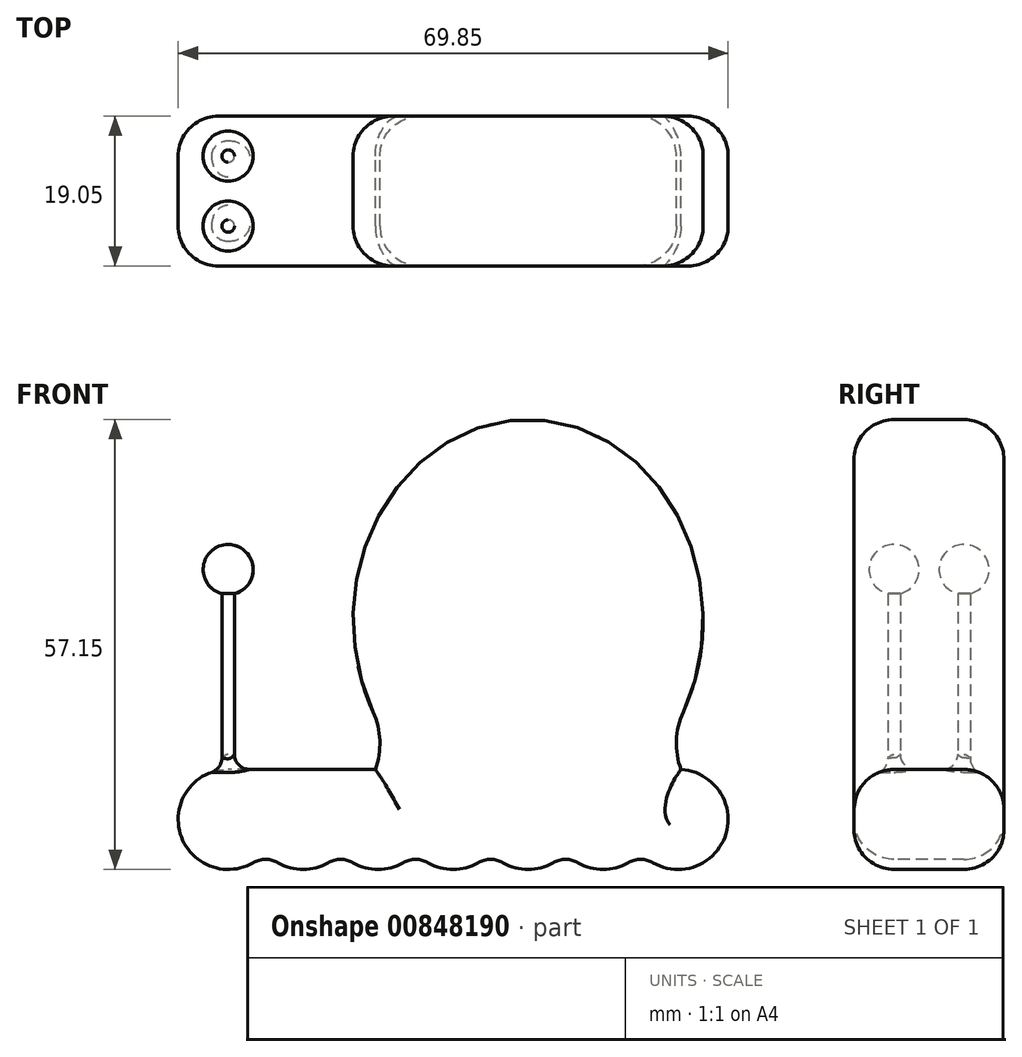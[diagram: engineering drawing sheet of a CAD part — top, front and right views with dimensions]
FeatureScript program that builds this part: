
annotation { "Feature Type Name" : "Feature", "Feature Type Description" : "" }
export const myFeature = defineFeature(function(context is Context, id is Id, definition is map)
    precondition{}
    {
        {
            var Q0;
            Q0=qCreatedBy(makeId("Front.planeOp"),FACE);
            var sketch = newSketch(context, id + "F0", { "sketchPlane" : qUnion([Q0])});
            skEllipticalArc(sketch, "E0", {});
            skLineSegment(sketch, "E1", {"start": v(0, 0) * mm, "end": v(-18.88, 0) * mm});
            skLineSegment(sketch, "E2", {"start": v(0, 0) * mm, "end": v(18.88, 0) * mm});
            skArc(sketch, "E3", {"start": v(19.7, 13.64) * mm, "mid": v(18.89, 8.58) * mm, "end": v(20.78, 3.82) * mm});
            skArc(sketch, "E4", {"start": v(-20.78, 3.82) * mm, "mid": v(-18.89, 8.58) * mm, "end": v(-19.7, 13.64) * mm});
            skPoint(sketch, "E5.end.orphan", {"position": v(-22.23, 25.4) * mm});
            skPoint(sketch, "E6.orphan", {"position": v(0, 50.8) * mm});
            skPoint(sketch, "E7.visualSharp", {"position": v(-28.46, 0) * mm});
            skArc(sketch, "E7.filletArc", {"start": v(-20.78, 3.82) * mm, "mid": v(-21.02, 1.32) * mm, "end": v(-18.88, 0) * mm});
            skPoint(sketch, "E8.visualSharp", {"position": v(28.46, 0) * mm});
            skArc(sketch, "E8.filletArc", {"start": v(18.88, 0) * mm, "mid": v(21.02, 1.32) * mm, "end": v(20.78, 3.82) * mm});
            skArc(sketch, "E9", {"start": v(-6.35, 0) * mm, "mid": v(0, -6.35) * mm, "end": v(6.35, 0) * mm});
            skArc(sketch, "E10.1.0.0", {"start": v(3.17, 0) * mm, "mid": v(9.52, -6.35) * mm, "end": v(15.88, 0) * mm});
            skArc(sketch, "E10.2.0.0", {"start": v(12.7, 0) * mm, "mid": v(23.41, -4.62) * mm, "end": v(19.4, 6.34) * mm});
            skLineSegment(sketch, "E10.direction1", {"start": v(0, 0) * mm, "end": v(9.53, 0) * mm, "construction": true});
            skArc(sketch, "E11.1.0.0", {"start": v(-15.88, 0) * mm, "mid": v(-9.53, -6.35) * mm, "end": v(-3.17, 0) * mm});
            skArc(sketch, "E11.2.0.0", {"start": v(-19.4, 6.34) * mm, "mid": v(-23.41, -4.62) * mm, "end": v(-12.7, 0) * mm});
            skCircle(sketch, "E11.3.0.0", {"center": v(-28.58, 0) * mm, "radius": 6.35 * mm});
            skCircle(sketch, "E11.4.0.0", {"center": v(-38.1, 0) * mm, "radius": 6.35 * mm});
            skLineSegment(sketch, "E11.direction1", {"start": v(0, 0) * mm, "end": v(-9.53, 0) * mm, "construction": true});
            skLineSegment(sketch, "E12", {"start": v(-38.1, 6.35) * mm, "end": v(-19.4, 6.35) * mm});
            const initialGuessF0  = {"E0": [0, 0.0254, 0, 1, 0.0254, 0.022225, 4.23107215542133, 2.0521131517582556]};
            skSetInitialGuess(sketch, initialGuessF0);
            skSolve(sketch);
        }
        {
            var Q0;
            {var subQ15=sQuery(id+"F0.wireOp",EDGE,"E0");Q0=makeQuery(id+"F0.imprint","IMPRINT",FACE,{"disambiguationData":[TD([[makeQuery(id+"F0.imprint","IMPRINT",EDGE,{"derivedFrom":subQ15}),1.0]])]});}
            var Q1;
            {var subQ5=sQuery(id+"F0.wireOp",EDGE,"E8.filletArc");Q1=makeQuery(id+"F0.imprint","IMPRINT",FACE,{"disambiguationData":[TD([[makeQuery(id+"F0.imprint","IMPRINT",EDGE,{"derivedFrom":subQ5}),-1.0]])]});}
            var Q2;
            {var subQ0=sQuery(id+"F0.wireOp",EDGE,"E10.1.0.0");var subQ1=sQuery(id+"F0.wireOp",EDGE,"E2");var subQ2=makeQuery(id+"F0.imprint","INTERSECT",VERTEX,{"disambiguationData":[OD(1.0)],"derivedFrom":[subQ1,subQ0]});Q2=makeQuery(id+"F0.imprint","IMPRINT",FACE,{"disambiguationData":[TD([[makeQuery(id+"F0.imprint","IMPRINT",EDGE,{"disambiguationData":[TD([[subQ2,1.0]])],"derivedFrom":subQ1}),-1.0]])]});}
            var Q3;
            {var subQ0=sQuery(id+"F0.wireOp",EDGE,"E9");var subQ1=sQuery(id+"F0.wireOp",EDGE,"E2");var subQ2=makeQuery(id+"F0.imprint","INTERSECT",VERTEX,{"derivedFrom":[subQ1,subQ0]});Q3=makeQuery(id+"F0.imprint","IMPRINT",FACE,{"disambiguationData":[TD([[makeQuery(id+"F0.imprint","IMPRINT",EDGE,{"disambiguationData":[TD([[subQ2,-1.0]])],"derivedFrom":subQ1}),-1.0]])]});}
            var Q4;
            {var subQ0=sQuery(id+"F0.wireOp",EDGE,"E9");var subQ1=sQuery(id+"F0.wireOp",EDGE,"E2");var subQ2=makeQuery(id+"F0.imprint","INTERSECT",VERTEX,{"derivedFrom":[subQ1,subQ0]});Q4=makeQuery(id+"F0.imprint","IMPRINT",FACE,{"disambiguationData":[TD([[makeQuery(id+"F0.imprint","IMPRINT",EDGE,{"disambiguationData":[TD([[subQ2,1.0]])],"derivedFrom":subQ1}),-1.0]])]});}
            var Q5;
            {var subQ5=sQuery(id+"F0.wireOp",EDGE,"E2");var subQ7=sQuery(id+"F0.wireOp",EDGE,"E1");var subQ8=makeQuery(id+"F0.imprint","INTERSECT",VERTEX,{"derivedFrom":[subQ7,subQ5]});Q5=makeQuery(id+"F0.imprint","IMPRINT",FACE,{"disambiguationData":[TD([[makeQuery(id+"F0.imprint","IMPRINT",EDGE,{"disambiguationData":[TD([[subQ8,-1.0]])],"derivedFrom":subQ7}),1.0]])]});}
            var Q6;
            {var subQ0=sQuery(id+"F0.wireOp",EDGE,"E9");var subQ1=sQuery(id+"F0.wireOp",EDGE,"E1");var subQ2=makeQuery(id+"F0.imprint","INTERSECT",VERTEX,{"derivedFrom":[subQ1,subQ0]});Q6=makeQuery(id+"F0.imprint","IMPRINT",FACE,{"disambiguationData":[TD([[makeQuery(id+"F0.imprint","IMPRINT",EDGE,{"disambiguationData":[TD([[subQ2,1.0]])],"derivedFrom":subQ1}),1.0]])]});}
            var Q7;
            {var subQ0=sQuery(id+"F0.wireOp",EDGE,"E9");var subQ1=sQuery(id+"F0.wireOp",EDGE,"E1");var subQ2=makeQuery(id+"F0.imprint","INTERSECT",VERTEX,{"derivedFrom":[subQ1,subQ0]});Q7=makeQuery(id+"F0.imprint","IMPRINT",FACE,{"disambiguationData":[TD([[makeQuery(id+"F0.imprint","IMPRINT",EDGE,{"disambiguationData":[TD([[subQ2,-1.0]])],"derivedFrom":subQ1}),1.0]])]});}
            var Q8;
            {var subQ0=sQuery(id+"F0.wireOp",EDGE,"E11.1.0.0");var subQ1=sQuery(id+"F0.wireOp",EDGE,"E1");var subQ2=makeQuery(id+"F0.imprint","INTERSECT",VERTEX,{"disambiguationData":[OD(0.0)],"derivedFrom":[subQ1,subQ0]});Q8=makeQuery(id+"F0.imprint","IMPRINT",FACE,{"disambiguationData":[TD([[makeQuery(id+"F0.imprint","IMPRINT",EDGE,{"disambiguationData":[TD([[subQ2,1.0]])],"derivedFrom":subQ1}),1.0]])]});}
            var Q9;
            {var subQ8=sQuery(id+"F0.wireOp",EDGE,"E7.filletArc");Q9=makeQuery(id+"F0.imprint","IMPRINT",FACE,{"disambiguationData":[TD([[makeQuery(id+"F0.imprint","IMPRINT",EDGE,{"derivedFrom":subQ8}),-1.0]])]});}
            var Q10;
            {var subQ0=sQuery(id+"F0.wireOp",EDGE,"E11.3.0.0");var subQ1=sQuery(id+"F0.wireOp",EDGE,"E11.2.0.0");var subQ2=makeQuery(id+"F0.imprint","INTERSECT",VERTEX,{"disambiguationData":[OD(0.0)],"derivedFrom":[subQ1,subQ0]});Q10=makeQuery(id+"F0.imprint","IMPRINT",FACE,{"disambiguationData":[TD([[makeQuery(id+"F0.imprint","IMPRINT",EDGE,{"disambiguationData":[TD([[subQ2,1.0]])],"derivedFrom":subQ1}),1.0]])]});}
            var Q11;
            {var subQ0=sQuery(id+"F0.wireOp",EDGE,"E11.3.0.0");var subQ1=sQuery(id+"F0.wireOp",EDGE,"E11.2.0.0");var subQ2=makeQuery(id+"F0.imprint","INTERSECT",VERTEX,{"disambiguationData":[OD(0.0)],"derivedFrom":[subQ1,subQ0]});Q11=makeQuery(id+"F0.imprint","IMPRINT",FACE,{"disambiguationData":[TD([[makeQuery(id+"F0.imprint","IMPRINT",EDGE,{"disambiguationData":[TD([[subQ2,1.0]])],"derivedFrom":subQ1}),-1.0]])]});}
            var Q12;
            {var subQ0=sQuery(id+"F0.wireOp",EDGE,"E11.4.0.0");var subQ1=sQuery(id+"F0.wireOp",EDGE,"E11.3.0.0");var subQ2=makeQuery(id+"F0.imprint","INTERSECT",VERTEX,{"disambiguationData":[OD(0.0)],"derivedFrom":[subQ1,subQ0]});Q12=makeQuery(id+"F0.imprint","IMPRINT",FACE,{"disambiguationData":[TD([[makeQuery(id+"F0.imprint","IMPRINT",EDGE,{"disambiguationData":[TD([[subQ2,1.0]])],"derivedFrom":subQ1}),1.0]])]});}
            var Q13;
            {var subQ0=sQuery(id+"F0.wireOp",EDGE,"E11.4.0.0");var subQ1=sQuery(id+"F0.wireOp",EDGE,"E11.3.0.0");var subQ2=makeQuery(id+"F0.imprint","INTERSECT",VERTEX,{"disambiguationData":[OD(0.0)],"derivedFrom":[subQ1,subQ0]});Q13=makeQuery(id+"F0.imprint","IMPRINT",FACE,{"disambiguationData":[TD([[makeQuery(id+"F0.imprint","IMPRINT",EDGE,{"disambiguationData":[TD([[subQ2,1.0]])],"derivedFrom":subQ1}),-1.0]])]});}
            var Q14;
            {var subQ0=sQuery(id+"F0.wireOp",EDGE,"E12");var subQ1=sQuery(id+"F0.wireOp",EDGE,"E11.3.0.0");var subQ2=makeQuery(id+"F0.imprint","INTERSECT",VERTEX,{"derivedFrom":[subQ1,subQ0]});Q14=makeQuery(id+"F0.imprint","IMPRINT",FACE,{"disambiguationData":[TD([[makeQuery(id+"F0.imprint","IMPRINT",EDGE,{"disambiguationData":[TD([[subQ2,-1.0]])],"derivedFrom":subQ1}),-1.0]])]});}
            var Q15;
            {var subQ0=sQuery(id+"F0.wireOp",EDGE,"E11.2.0.0");var subQ1=sQuery(id+"F0.wireOp",EDGE,"E4");var subQ2=makeQuery(id+"F0.imprint","INTERSECT",VERTEX,{"derivedFrom":[subQ1,subQ0]});Q15=makeQuery(id+"F0.imprint","IMPRINT",FACE,{"disambiguationData":[TD([[makeQuery(id+"F0.imprint","IMPRINT",EDGE,{"disambiguationData":[TD([[subQ2,-1.0]])],"derivedFrom":subQ1}),1.0]])]});}
            extrude(context, id + "F1", {"entities" : qUnion([Q0, Q1, Q2, Q3, Q4, Q5, Q6, Q7, Q8, Q9, Q10, Q11, Q12, Q13, Q14, Q15]), "depth" : 19.05 * mm, "offsetDistance" : 25.4 * mm});
        }
        {
            var Q0;
            Q0=makeQuery(id+"F1.opExtrude","SWEPT_EDGE",EDGE,{"disambiguationData":[OSD([sQuery(id+"F0.wireOp",EDGE,"E11.3.0.0"),sQuery(id+"F0.wireOp",EDGE,"E11.4.0.0")])]});
            var Q1;
            Q1=makeQuery(id+"F1.opExtrude","SWEPT_EDGE",EDGE,{"disambiguationData":[OSD([sQuery(id+"F0.wireOp",EDGE,"E11.2.0.0"),sQuery(id+"F0.wireOp",EDGE,"E11.3.0.0")])]});
            var Q2;
            Q2=makeQuery(id+"F1.opExtrude","SWEPT_EDGE",EDGE,{"disambiguationData":[OSD([sQuery(id+"F0.wireOp",EDGE,"E11.1.0.0"),sQuery(id+"F0.wireOp",EDGE,"E11.2.0.0")])]});
            var Q3;
            Q3=makeQuery(id+"F1.opExtrude","SWEPT_EDGE",EDGE,{"disambiguationData":[OSD([sQuery(id+"F0.wireOp",EDGE,"E9"),sQuery(id+"F0.wireOp",EDGE,"E11.1.0.0")])]});
            var Q4;
            Q4=makeQuery(id+"F1.opExtrude","SWEPT_EDGE",EDGE,{"disambiguationData":[OSD([sQuery(id+"F0.wireOp",EDGE,"E9"),sQuery(id+"F0.wireOp",EDGE,"E10.1.0.0")])]});
            var Q5;
            Q5=makeQuery(id+"F1.opExtrude","SWEPT_EDGE",EDGE,{"disambiguationData":[OSD([sQuery(id+"F0.wireOp",EDGE,"E10.1.0.0"),sQuery(id+"F0.wireOp",EDGE,"E10.2.0.0")])]});
            fillet(context, id + "F2", {"entities" : qUnion([Q0, Q1, Q2, Q3, Q4, Q5]), "radius" : 3.17 * mm, "tangentPropagation" : true, "allowEdgeOverflow" : false});
        }
        {
            var Q0;
            Q0=makeQuery(id+"F1.opExtrude","CAP_EDGE",EDGE,{"disambiguationData":[OSD([sQuery(id+"F0.wireOp",EDGE,"E0")])],"isStart":false});
            var Q1;
            Q1=makeQuery(id+"F1.opExtrude","CAP_EDGE",EDGE,{"disambiguationData":[OSD([sQuery(id+"F0.wireOp",EDGE,"E0")])],"isStart":true});
            fillet(context, id + "F3", {"entities" : qUnion([Q0, Q1]), "radius" : 5.08 * mm, "tangentPropagation" : true, "allowEdgeOverflow" : false});
        }
        {
            var Q0;
            Q0=makeQuery(id+"F1.opExtrude","CAP_FACE",FACE,{"disambiguationData":[OSD([sQuery(id+"F0.wireOp",EDGE,"E0"),sQuery(id+"F0.wireOp",EDGE,"E3"),sQuery(id+"F0.wireOp",EDGE,"E4"),sQuery(id+"F0.wireOp",EDGE,"E9"),sQuery(id+"F0.wireOp",EDGE,"E10.1.0.0"),sQuery(id+"F0.wireOp",EDGE,"E10.2.0.0"),sQuery(id+"F0.wireOp",EDGE,"E11.1.0.0"),sQuery(id+"F0.wireOp",EDGE,"E11.2.0.0"),sQuery(id+"F0.wireOp",EDGE,"E11.3.0.0"),sQuery(id+"F0.wireOp",EDGE,"E11.4.0.0"),sQuery(id+"F0.wireOp",EDGE,"E12")])],"isStart":false});
            var Q1;
            Q1=makeQuery(id+"F1.opExtrude","CAP_FACE",FACE,{"disambiguationData":[OSD([sQuery(id+"F0.wireOp",EDGE,"E0"),sQuery(id+"F0.wireOp",EDGE,"E3"),sQuery(id+"F0.wireOp",EDGE,"E4"),sQuery(id+"F0.wireOp",EDGE,"E9"),sQuery(id+"F0.wireOp",EDGE,"E10.1.0.0"),sQuery(id+"F0.wireOp",EDGE,"E10.2.0.0"),sQuery(id+"F0.wireOp",EDGE,"E11.1.0.0"),sQuery(id+"F0.wireOp",EDGE,"E11.2.0.0"),sQuery(id+"F0.wireOp",EDGE,"E11.3.0.0"),sQuery(id+"F0.wireOp",EDGE,"E11.4.0.0"),sQuery(id+"F0.wireOp",EDGE,"E12")])],"isStart":true});
            fillet(context, id + "F4", {"entities" : qUnion([Q0, Q1]), "radius" : 5.08 * mm, "tangentPropagation" : true, "allowEdgeOverflow" : false});
        }
        {
            var Q0;
            Q0=makeQuery(id+"F1.opExtrude","SWEPT_FACE",FACE,{"disambiguationData":[OSD([sQuery(id+"F0.wireOp",EDGE,"E12")])]});
            var sketch = newSketch(context, id + "F5", { "sketchPlane" : qUnion([Q0])});
            skCircle(sketch, "E13", {"center": v(-38.1, -5.08) * mm, "radius": 0.8 * mm});
            skCircle(sketch, "E14", {"center": v(-38.1, -13.97) * mm, "radius": 0.8 * mm});
            skSolve(sketch);
        }
        {
            var Q0;
            Q0 = qSketchRegion(id + "F5", true);
            extrude(context, id + "F6", {"entities" : qUnion([Q0]), "operationType" : NewBodyOperationType.ADD, "depth" : 25.4 * mm, "offsetDistance" : 25.4 * mm, "hasSecondDirection" : true, "secondDirectionBound" : SecondDirectionBoundingType.UP_TO_NEXT, "secondDirectionOppositeDirection" : true, "secondDirectionDepth" : 25.4 * mm});
        }
        {
            var Q0;
            Q0=makeQuery(id+"F1.opExtrude","CAP_FACE",FACE,{"disambiguationData":[OSD([sQuery(id+"F0.wireOp",EDGE,"E0"),sQuery(id+"F0.wireOp",EDGE,"E3"),sQuery(id+"F0.wireOp",EDGE,"E4"),sQuery(id+"F0.wireOp",EDGE,"E9"),sQuery(id+"F0.wireOp",EDGE,"E10.1.0.0"),sQuery(id+"F0.wireOp",EDGE,"E10.2.0.0"),sQuery(id+"F0.wireOp",EDGE,"E11.1.0.0"),sQuery(id+"F0.wireOp",EDGE,"E11.2.0.0"),sQuery(id+"F0.wireOp",EDGE,"E11.3.0.0"),sQuery(id+"F0.wireOp",EDGE,"E11.4.0.0"),sQuery(id+"F0.wireOp",EDGE,"E12")])],"isStart":false});
            cPlane(context, id + "F7", {"entities" : qUnion([Q0]), "cplaneType" : CPlaneType.OFFSET, "offset" : 5.08 * mm, "oppositeDirection" : true, "width" : 152.4 * mm, "height" : 152.4 * mm});
        }
        {
            var Q0;
            Q0=qCreatedBy(id+"F7.planeOp",FACE);
            var sketch = newSketch(context, id + "F8", { "sketchPlane" : qUnion([Q0])});
            skLineSegment(sketch, "E15", {"start": v(-37.3, 31.75) * mm, "end": v(-37.3, 6.35) * mm});
            skLineSegment(sketch, "E16.0", {"start": v(-38.9, 31.75) * mm, "end": v(-37.3, 31.75) * mm});
            skArc(sketch, "E17", {"start": v(-38.1, 34.93) * mm, "mid": v(-41.25, 32.15) * mm, "end": v(-38.9, 28.68) * mm});
            skLineSegment(sketch, "E18", {"start": v(-38.1, 31.75) * mm, "end": v(-38.1, 34.93) * mm});
            skLineSegment(sketch, "E19", {"start": v(-38.9, 6.15) * mm, "end": v(-38.9, 31.75) * mm});
            skSolve(sketch);
        }
        {
            var Q0;
            {var subQ4=sQuery(id+"F8.wireOp",EDGE,"E17");Q0=makeQuery(id+"F8.imprint","IMPRINT",FACE,{"disambiguationData":[TD([[makeQuery(id+"F8.imprint","IMPRINT",EDGE,{"derivedFrom":subQ4}),1.0]])]});}
            var Q1;
            Q1=sQuery(id+"F8.wireOp",EDGE,"E18");
            revolve(context, id + "F9", {"operationType" : NewBodyOperationType.ADD, "surfaceOperationType" : NewSurfaceOperationType.NEW, "entities" : qUnion([Q0]), "axis" : qUnion([Q1]), "revolveType" : RevolveType.FULL});
        }
        {
            var Q0;
            Q0=makeQuery(id+"F1.opExtrude","CAP_FACE",FACE,{"disambiguationData":[OSD([sQuery(id+"F0.wireOp",EDGE,"E0"),sQuery(id+"F0.wireOp",EDGE,"E3"),sQuery(id+"F0.wireOp",EDGE,"E4"),sQuery(id+"F0.wireOp",EDGE,"E9"),sQuery(id+"F0.wireOp",EDGE,"E10.1.0.0"),sQuery(id+"F0.wireOp",EDGE,"E10.2.0.0"),sQuery(id+"F0.wireOp",EDGE,"E11.1.0.0"),sQuery(id+"F0.wireOp",EDGE,"E11.2.0.0"),sQuery(id+"F0.wireOp",EDGE,"E11.3.0.0"),sQuery(id+"F0.wireOp",EDGE,"E11.4.0.0"),sQuery(id+"F0.wireOp",EDGE,"E12")])],"isStart":true});
            cPlane(context, id + "F10", {"entities" : qUnion([Q0]), "cplaneType" : CPlaneType.OFFSET, "offset" : 5.08 * mm, "oppositeDirection" : true, "width" : 152.4 * mm, "height" : 152.4 * mm});
        }
        {
            var Q0;
            Q0=qCreatedBy(id+"F10.planeOp",FACE);
            var sketch = newSketch(context, id + "F11", { "sketchPlane" : qUnion([Q0])});
            skLineSegment(sketch, "E20", {"start": v(38.9, 31.75) * mm, "end": v(38.9, 6.24) * mm});
            skLineSegment(sketch, "E21.0", {"start": v(38.1, 31.75) * mm, "end": v(38.9, 31.75) * mm});
            skArc(sketch, "E22", {"start": v(38.9, 28.68) * mm, "mid": v(41.25, 32.15) * mm, "end": v(38.1, 34.93) * mm});
            skLineSegment(sketch, "E23", {"start": v(38.1, 31.75) * mm, "end": v(38.1, 34.93) * mm});
            skPoint(sketch, "E24.orphan", {"position": v(37.3, 31.75) * mm});
            skSolve(sketch);
        }
        {
            var Q0;
            Q0 = qSketchRegion(id + "F11", true);
            var Q1;
            Q1=sQuery(id+"F11.wireOp",EDGE,"E23");
            revolve(context, id + "F12", {"operationType" : NewBodyOperationType.ADD, "surfaceOperationType" : NewSurfaceOperationType.NEW, "entities" : qUnion([Q0]), "axis" : qUnion([Q1]), "revolveType" : RevolveType.FULL});
        }
        {
            var Q0;
            {var subQ0=sQuery(id+"F0.wireOp",EDGE,"E11.4.0.0");Q0=makeQuery(id+"F6.boolean.opBoolean","INTERSECT",EDGE,{"derivedFrom":[makeQuery(id+"F4.opFillet","BLEND_FACE",FACE,{"disambiguationData":[OSD([subQ0]),TDD([makeQuery(id+"F1.opExtrude","CAP_EDGE",EDGE,{"disambiguationData":[OSD([subQ0])],"isStart":true})])]}),makeQuery(id+"F6.opExtrude","SWEPT_FACE",FACE,{"disambiguationData":[OSD([sQuery(id+"F5.wireOp",EDGE,"E13")])]})]});}
            var Q1;
            Q1=makeQuery(id+"F6.boolean.opBoolean","INTERSECT",EDGE,{"derivedFrom":[makeQuery(id+"F1.opExtrude","SWEPT_FACE",FACE,{"disambiguationData":[OSD([sQuery(id+"F0.wireOp",EDGE,"E11.4.0.0")])]}),makeQuery(id+"F6.opExtrude","SWEPT_FACE",FACE,{"disambiguationData":[OSD([sQuery(id+"F5.wireOp",EDGE,"E14")])]})]});
            fillet(context, id + "F13", {"entities" : qUnion([Q0, Q1]), "radius" : 1.9 * mm, "tangentPropagation" : true, "allowEdgeOverflow" : false});
        }
    });
